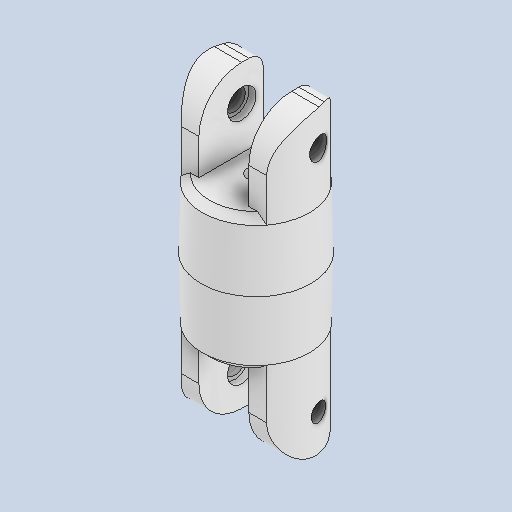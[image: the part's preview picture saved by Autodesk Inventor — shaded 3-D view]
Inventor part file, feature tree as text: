
AUTODESK INVENTOR PART (.ipt)
format: ipt  version: 2022 (Build 260153000, 153)  size: 285,184 bytes
history: native  units: in
note: dims shown in document units (in); Inventor stores cm internally (conversion verified against a paired STEP export)
features: sketch x10, extrude x6, fillet x5, hole x4, chamfer x4, thread x4
ambient origin geometry x8: Origin, YZ Plane, XZ Plane, XY Plane, X Axis, Y Axis, Z Axis, Center Point
bodies: Solid1 (feature_tree)
feature tree (33):
  extrude  "Extrusion1"  Depth=0.0984in
  extrude  "Extrusion2"  Depth=0.2362in
  fillet  "Fillet1"  Radius=0.0787in
  fillet  "Fillet2"  Radius=0.1969in
  hole  "Hole1"  [1 undecoded]
  hole  "Hole2"  [1 undecoded]
  extrude  "Extrusion3"  Depth=0.3346in TaperAngle=45.0deg
  chamfer  "Chamfer1"  Distance=0.3346in
  extrude  "Extrusion4"  Depth=0.0394in TaperAngle=0.0deg
  chamfer  "Chamfer2"  Distance=0.0394in Angle=45.0deg
  extrude  "Extrusion5"  Depth=0.4331in TaperAngle=0.0deg
  chamfer  "Chamfer3"  Distance=0.1969in
  fillet  "Fillet3"  Radius=0.0394in
  fillet  "Fillet4"  Radius=0.2362in
  fillet  "Fillet5"  Radius=0.2362in
  hole  "Hole3"  [1 undecoded]
  hole  "Hole4"  [1 undecoded]
  chamfer  "Chamfer4"  [1 undecoded]
  thread  "Thread1"  [1 undecoded]
  thread  "Thread2"  [1 undecoded]
  thread  "Thread3"  [1 undecoded]
  thread  "Thread4"  [1 undecoded]
  sketch  "Sketch1"  dims[d5=0.4724in d6=0.0in d7=0.0984in]
  sketch  "Sketch2"  dims[d8=0.0394in d9=0.0in d10=0.2362in d11=0.0787in d16=0.1969in]
  sketch  "Sketch3"  dims[d17=0.0984in d18=0.2362in d19=0.1575in d20=0.0394in d21=90.0deg d22=0.1575in d23=0.0in d24=0.1969in]
  sketch  "Sketch4"  dims[d25=0.1181in d26=0.2362in d27=0.1575in d28=0.0394in d29=90.0deg d30=0.1575in d31=0.0in d32=0.6063in]
  sketch  "Sketch5"  dims[d33=0.3346in d34=0.0in d35=0.3346in d36=0.0079in d37=45.0deg d38=0.3346in d39=0.0in]
  sketch  "Sketch6"  dims[d40=0.0079in d41=0.3346in d42=45.0deg d43=0.0394in d44=0.0in d45=0.0394in d46=0.3346in d47=45.0deg]
  sketch  "Sketch7"  dims[d48=0.0394in d50=0.0in d51=0.4331in]
  sketch  "Sketch9"  dims[d53=0.0787in]
  sketch  "Sketch10"  dims[d54=0.1969in d55=0.1181in d56=0.2362in d57=0.1575in d58=0.0394in d59=90.0deg d60=0.1575in d61=0.0in d62=0.1969in d63=0.1181in d64=0.2362in d65=0.1575in d66=0.0394in d67=90.0deg d68=0.1575in d69=0.0in d70=0.0394in d71=0.3346in d72=45.0deg d73=0.2362in d74=0.0in d75=0.2362in d76=0.0in d77=0.2362in d78=0.0in d79=0.2362in d80=0.0in d12=0.0in d13=0.0in]
  extrude  "Extrusion6"  [1 undecoded]
  sketch  "Sketch8"  dims[d52=0.2362in]
note: 10 required parameter values undecoded (feature->parameter linkage not recoverable at this tier; creation-order binding heuristic only, values carry confidence <= 0.55)
